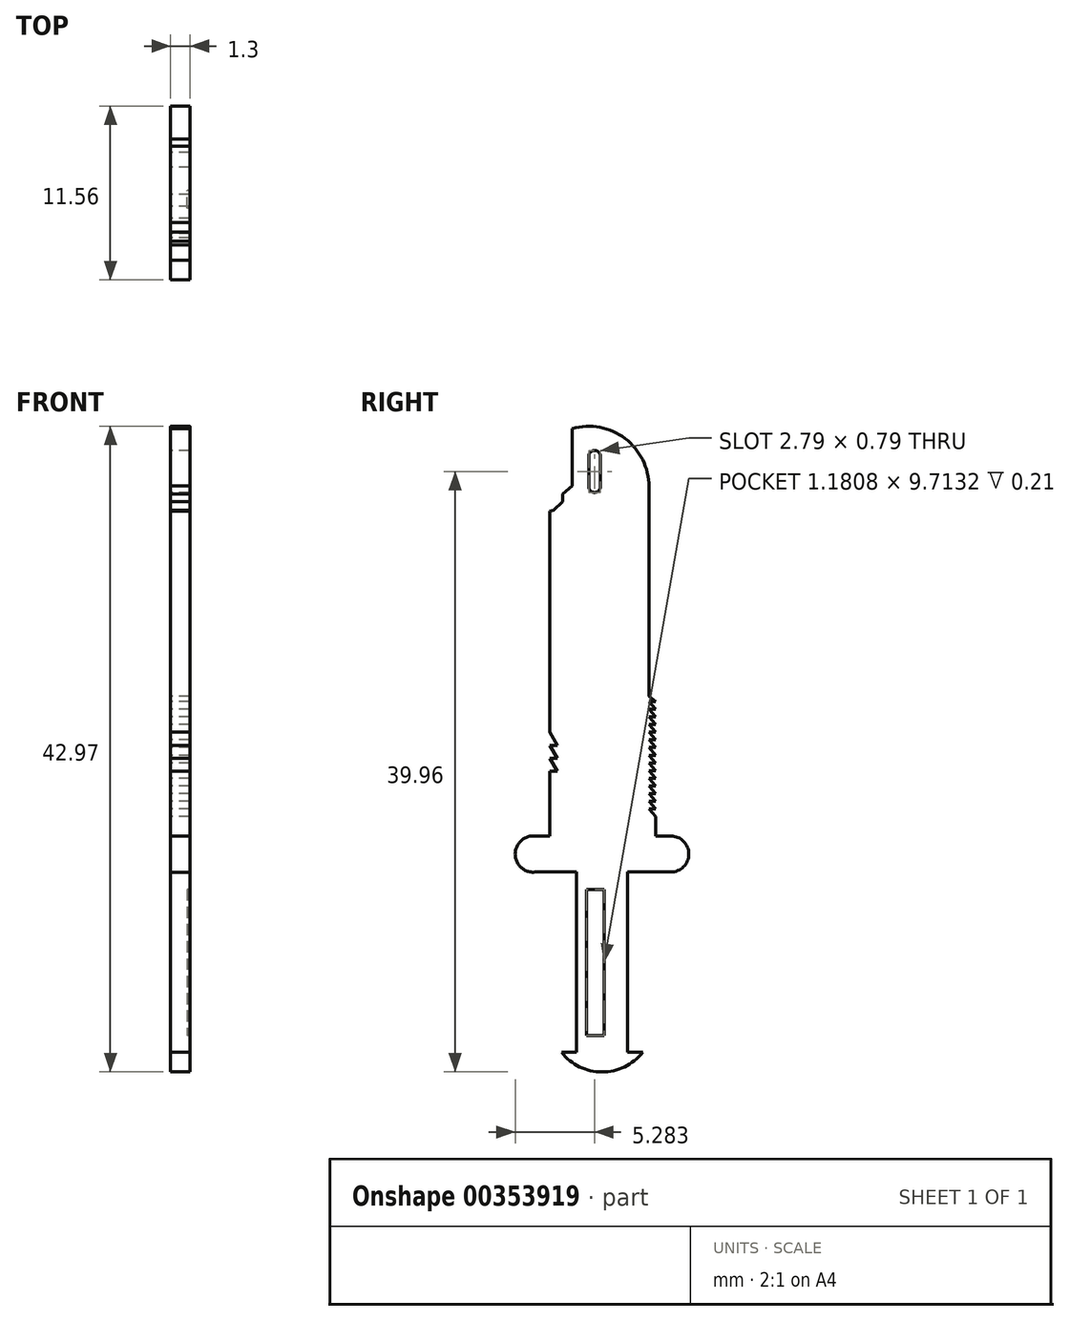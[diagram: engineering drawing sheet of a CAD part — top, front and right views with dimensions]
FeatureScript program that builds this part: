
annotation { "Feature Type Name" : "Feature", "Feature Type Description" : "" }
export const myFeature = defineFeature(function(context is Context, id is Id, definition is map)
    precondition{}
    {
        {
            var Q0;
            Q0=qCreatedBy(makeId("Right.planeOp"),FACE);
            var sketch = newSketch(context, id + "F0", { "sketchPlane" : qUnion([Q0])});
            skLineSegment(sketch, "E0", {"start": v(-45.92, 24.34) * mm, "end": v(-45.92, 12.34) * mm});
            skLineSegment(sketch, "E1", {"start": v(-45.92, 12.34) * mm, "end": v(-46.92, 12.34) * mm});
            skLineSegment(sketch, "E2", {"start": v(-41.52, 12.34) * mm, "end": v(-42.52, 12.34) * mm});
            skLineSegment(sketch, "E3", {"start": v(-42.52, 12.34) * mm, "end": v(-42.52, 24.34) * mm});
            skLineSegment(sketch, "E4", {"start": v(-47.7, 48.37) * mm, "end": v(-47.44, 48.43) * mm});
            skLineSegment(sketch, "E5", {"start": v(-47.44, 48.43) * mm, "end": v(-46.83, 49) * mm});
            skLineSegment(sketch, "E6", {"start": v(-46.83, 49) * mm, "end": v(-46.83, 49.5) * mm});
            skLineSegment(sketch, "E7", {"start": v(-46.83, 49.5) * mm, "end": v(-46.2, 50.05) * mm});
            skLineSegment(sketch, "E8", {"start": v(-46.2, 50.05) * mm, "end": v(-46.2, 50.86) * mm});
            skLineSegment(sketch, "E9", {"start": v(-46.2, 50.86) * mm, "end": v(-46.2, 53.86) * mm});
            skLineSegment(sketch, "E10", {"start": v(-46.2, 53.86) * mm, "end": v(-45.44, 53.86) * mm});
            skLineSegment(sketch, "E11", {"start": v(-45.44, 53.86) * mm, "end": v(-44.86, 53.5) * mm});
            skLineSegment(sketch, "E12", {"start": v(-44.86, 53.5) * mm, "end": v(-43.98, 52.87) * mm});
            skLineSegment(sketch, "E13", {"start": v(-43.98, 52.87) * mm, "end": v(-42.83, 51.88) * mm});
            skLineSegment(sketch, "E14", {"start": v(-42.83, 51.88) * mm, "end": v(-42.23, 50.74) * mm});
            skLineSegment(sketch, "E15", {"start": v(-42.23, 50.74) * mm, "end": v(-42.23, 49.66) * mm});
            skLineSegment(sketch, "E16", {"start": v(-42.23, 49.66) * mm, "end": v(-42.23, 48.37) * mm});
            skLineSegment(sketch, "E17", {"start": v(-42.23, 48.37) * mm, "end": v(-42.23, 47.61) * mm});
            skLineSegment(sketch, "E18", {"start": v(-42.23, 47.61) * mm, "end": v(-42.23, 36.92) * mm});
            skLineSegment(sketch, "E19", {"start": v(-42.23, 36.92) * mm, "end": v(-40.64, 35.69) * mm});
            skLineSegment(sketch, "E20", {"start": v(-40.64, 35.69) * mm, "end": v(-41.1, 35.7) * mm});
            skLineSegment(sketch, "E21", {"start": v(-41.1, 35.7) * mm, "end": v(-40.64, 35.17) * mm});
            skLineSegment(sketch, "E22", {"start": v(-40.64, 35.17) * mm, "end": v(-41.1, 35.17) * mm});
            skLineSegment(sketch, "E23", {"start": v(-41.1, 35.17) * mm, "end": v(-40.64, 34.66) * mm});
            skLineSegment(sketch, "E24", {"start": v(-40.64, 34.66) * mm, "end": v(-41.1, 34.66) * mm});
            skLineSegment(sketch, "E25", {"start": v(-41.1, 34.66) * mm, "end": v(-40.64, 34.15) * mm});
            skLineSegment(sketch, "E26", {"start": v(-40.64, 34.15) * mm, "end": v(-41.1, 34.15) * mm});
            skLineSegment(sketch, "E27", {"start": v(-41.1, 34.15) * mm, "end": v(-40.64, 33.64) * mm});
            skLineSegment(sketch, "E28", {"start": v(-40.64, 33.64) * mm, "end": v(-41.1, 33.64) * mm});
            skLineSegment(sketch, "E29", {"start": v(-41.1, 33.64) * mm, "end": v(-40.64, 33.14) * mm});
            skLineSegment(sketch, "E30", {"start": v(-40.64, 33.14) * mm, "end": v(-41.1, 33.14) * mm});
            skLineSegment(sketch, "E31", {"start": v(-41.1, 33.14) * mm, "end": v(-40.64, 32.63) * mm});
            skLineSegment(sketch, "E32", {"start": v(-40.64, 32.63) * mm, "end": v(-41.1, 32.63) * mm});
            skLineSegment(sketch, "E33", {"start": v(-41.1, 32.63) * mm, "end": v(-40.64, 32.12) * mm});
            skLineSegment(sketch, "E34", {"start": v(-40.64, 32.12) * mm, "end": v(-41.1, 32.12) * mm});
            skLineSegment(sketch, "E35", {"start": v(-41.1, 32.12) * mm, "end": v(-40.64, 31.6) * mm});
            skLineSegment(sketch, "E36", {"start": v(-40.64, 31.6) * mm, "end": v(-41.1, 31.6) * mm});
            skLineSegment(sketch, "E37", {"start": v(-41.1, 31.6) * mm, "end": v(-40.64, 31.1) * mm});
            skLineSegment(sketch, "E38", {"start": v(-40.64, 31.1) * mm, "end": v(-41.1, 31.1) * mm});
            skLineSegment(sketch, "E39", {"start": v(-41.1, 31.1) * mm, "end": v(-40.64, 30.6) * mm});
            skLineSegment(sketch, "E40", {"start": v(-40.64, 30.6) * mm, "end": v(-41.1, 30.6) * mm});
            skLineSegment(sketch, "E41", {"start": v(-41.1, 30.6) * mm, "end": v(-40.64, 30.08) * mm});
            skLineSegment(sketch, "E42", {"start": v(-40.64, 30.08) * mm, "end": v(-41.1, 30.08) * mm});
            skLineSegment(sketch, "E43", {"start": v(-41.1, 30.08) * mm, "end": v(-40.64, 29.58) * mm});
            skLineSegment(sketch, "E44", {"start": v(-40.64, 29.58) * mm, "end": v(-41.1, 29.58) * mm});
            skLineSegment(sketch, "E45", {"start": v(-41.1, 29.58) * mm, "end": v(-40.64, 29.07) * mm});
            skLineSegment(sketch, "E46", {"start": v(-40.64, 29.07) * mm, "end": v(-41.1, 29.07) * mm});
            skLineSegment(sketch, "E47", {"start": v(-41.1, 29.07) * mm, "end": v(-40.64, 28.56) * mm});
            skLineSegment(sketch, "E48", {"start": v(-40.64, 28.56) * mm, "end": v(-41.1, 28.56) * mm});
            skLineSegment(sketch, "E49", {"start": v(-41.1, 28.56) * mm, "end": v(-40.64, 28.05) * mm});
            skLineSegment(sketch, "E50", {"start": v(-40.64, 28.05) * mm, "end": v(-40.64, 26.74) * mm});
            skLineSegment(sketch, "E51", {"start": v(-47.7, 26.74) * mm, "end": v(-40.64, 26.74) * mm});
            skLineSegment(sketch, "E52", {"start": v(-45.92, 24.34) * mm, "end": v(-42.52, 24.34) * mm});
            skLineSegment(sketch, "E53", {"start": v(-45.92, 12.34) * mm, "end": v(-42.52, 12.34) * mm});
            skLineSegment(sketch, "E54", {"start": v(-41.1, 36.05) * mm, "end": v(-41.1, 50) * mm});
            skArc(sketch, "E55", {"start": v(-41.1, 50) * mm, "mid": v(-42.69, 53.2) * mm, "end": v(-46.2, 53.86) * mm});
            skLineSegment(sketch, "E56", {"start": v(-45.11, 50) * mm, "end": v(-45.11, 52) * mm});
            skArc(sketch, "E57", {"start": v(-45.11, 50) * mm, "mid": v(-44.72, 49.6) * mm, "end": v(-44.32, 50) * mm});
            skLineSegment(sketch, "E58", {"start": v(-44.32, 50) * mm, "end": v(-44.32, 52) * mm});
            skArc(sketch, "E59", {"start": v(-44.32, 52) * mm, "mid": v(-44.72, 52.4) * mm, "end": v(-45.11, 52) * mm});
            skLineSegment(sketch, "E60.bottom", {"start": v(-45.26, 23.19) * mm, "end": v(-44.07, 23.19) * mm});
            skLineSegment(sketch, "E60.top", {"start": v(-45.26, 13.47) * mm, "end": v(-44.07, 13.47) * mm});
            skLineSegment(sketch, "E60.left", {"start": v(-45.26, 23.19) * mm, "end": v(-45.26, 13.47) * mm});
            skLineSegment(sketch, "E60.right", {"start": v(-44.07, 23.19) * mm, "end": v(-44.07, 13.47) * mm});
            skLineSegment(sketch, "E61", {"start": v(-42.52, 23.19) * mm, "end": v(-42.92, 23.19) * mm});
            skLineSegment(sketch, "E62", {"start": v(-42.92, 23.19) * mm, "end": v(-42.52, 23.19) * mm});
            skLineSegment(sketch, "E63", {"start": v(-42.52, 23.19) * mm, "end": v(-42.52, 22.89) * mm});
            skLineSegment(sketch, "E64", {"start": v(-42.52, 22.89) * mm, "end": v(-42.92, 22.89) * mm});
            skLineSegment(sketch, "E65", {"start": v(-42.92, 22.89) * mm, "end": v(-42.52, 22.89) * mm});
            skLineSegment(sketch, "E66", {"start": v(-42.52, 22.89) * mm, "end": v(-42.52, 22.59) * mm});
            skLineSegment(sketch, "E67", {"start": v(-42.52, 22.59) * mm, "end": v(-42.92, 22.59) * mm});
            skLineSegment(sketch, "E68", {"start": v(-42.92, 22.59) * mm, "end": v(-42.52, 22.59) * mm});
            skLineSegment(sketch, "E69", {"start": v(-42.52, 22.59) * mm, "end": v(-42.52, 22.29) * mm});
            skLineSegment(sketch, "E70", {"start": v(-42.52, 22.29) * mm, "end": v(-42.92, 22.29) * mm});
            skLineSegment(sketch, "E71", {"start": v(-42.92, 22.29) * mm, "end": v(-42.52, 22.29) * mm});
            skLineSegment(sketch, "E72", {"start": v(-42.52, 22.29) * mm, "end": v(-42.52, 21.99) * mm});
            skLineSegment(sketch, "E73", {"start": v(-42.52, 21.99) * mm, "end": v(-42.92, 21.99) * mm});
            skLineSegment(sketch, "E74", {"start": v(-42.92, 21.99) * mm, "end": v(-42.52, 21.99) * mm});
            skLineSegment(sketch, "E75", {"start": v(-42.52, 21.99) * mm, "end": v(-42.52, 21.69) * mm});
            skLineSegment(sketch, "E76", {"start": v(-42.52, 21.69) * mm, "end": v(-42.92, 21.69) * mm});
            skLineSegment(sketch, "E77", {"start": v(-42.92, 21.69) * mm, "end": v(-42.52, 21.69) * mm});
            skLineSegment(sketch, "E78", {"start": v(-42.52, 21.69) * mm, "end": v(-42.52, 21.39) * mm});
            skLineSegment(sketch, "E79", {"start": v(-42.52, 21.39) * mm, "end": v(-42.92, 21.39) * mm});
            skLineSegment(sketch, "E80", {"start": v(-42.92, 21.39) * mm, "end": v(-42.52, 21.39) * mm});
            skLineSegment(sketch, "E81", {"start": v(-42.52, 21.39) * mm, "end": v(-42.52, 21.09) * mm});
            skLineSegment(sketch, "E82", {"start": v(-42.52, 21.09) * mm, "end": v(-42.92, 21.09) * mm});
            skLineSegment(sketch, "E83", {"start": v(-42.92, 21.09) * mm, "end": v(-42.52, 21.09) * mm});
            skLineSegment(sketch, "E84", {"start": v(-42.52, 21.09) * mm, "end": v(-42.52, 20.79) * mm});
            skLineSegment(sketch, "E85", {"start": v(-42.52, 20.79) * mm, "end": v(-42.92, 20.79) * mm});
            skLineSegment(sketch, "E86", {"start": v(-42.92, 20.79) * mm, "end": v(-42.52, 20.79) * mm});
            skLineSegment(sketch, "E87", {"start": v(-42.52, 20.79) * mm, "end": v(-42.52, 20.49) * mm});
            skLineSegment(sketch, "E88", {"start": v(-42.52, 20.49) * mm, "end": v(-42.92, 20.49) * mm});
            skLineSegment(sketch, "E89", {"start": v(-42.92, 20.49) * mm, "end": v(-42.52, 20.49) * mm});
            skLineSegment(sketch, "E90", {"start": v(-42.52, 20.49) * mm, "end": v(-42.52, 20.19) * mm});
            skLineSegment(sketch, "E91", {"start": v(-42.52, 20.19) * mm, "end": v(-42.92, 20.19) * mm});
            skLineSegment(sketch, "E92", {"start": v(-42.92, 20.19) * mm, "end": v(-42.52, 20.19) * mm});
            skLineSegment(sketch, "E93", {"start": v(-42.52, 20.19) * mm, "end": v(-42.52, 19.89) * mm});
            skLineSegment(sketch, "E94", {"start": v(-42.52, 19.89) * mm, "end": v(-42.92, 19.89) * mm});
            skLineSegment(sketch, "E95", {"start": v(-42.92, 19.89) * mm, "end": v(-42.52, 19.89) * mm});
            skLineSegment(sketch, "E96", {"start": v(-42.52, 19.89) * mm, "end": v(-42.52, 19.59) * mm});
            skLineSegment(sketch, "E97", {"start": v(-42.52, 19.59) * mm, "end": v(-42.92, 19.59) * mm});
            skLineSegment(sketch, "E98", {"start": v(-42.92, 19.59) * mm, "end": v(-42.52, 19.59) * mm});
            skLineSegment(sketch, "E99", {"start": v(-42.52, 19.59) * mm, "end": v(-42.52, 19.28) * mm});
            skLineSegment(sketch, "E100", {"start": v(-42.52, 19.28) * mm, "end": v(-42.92, 19.28) * mm});
            skLineSegment(sketch, "E101", {"start": v(-42.92, 19.28) * mm, "end": v(-42.52, 19.28) * mm});
            skLineSegment(sketch, "E102", {"start": v(-42.52, 19.28) * mm, "end": v(-42.52, 18.98) * mm});
            skLineSegment(sketch, "E103", {"start": v(-42.52, 18.98) * mm, "end": v(-42.92, 18.98) * mm});
            skLineSegment(sketch, "E104", {"start": v(-42.92, 18.98) * mm, "end": v(-42.52, 18.98) * mm});
            skLineSegment(sketch, "E105", {"start": v(-42.52, 18.98) * mm, "end": v(-42.52, 18.68) * mm});
            skLineSegment(sketch, "E106", {"start": v(-42.52, 18.68) * mm, "end": v(-42.92, 18.68) * mm});
            skLineSegment(sketch, "E107", {"start": v(-42.92, 18.68) * mm, "end": v(-42.52, 18.68) * mm});
            skLineSegment(sketch, "E108", {"start": v(-42.52, 18.68) * mm, "end": v(-42.52, 18.38) * mm});
            skLineSegment(sketch, "E109", {"start": v(-42.52, 18.38) * mm, "end": v(-42.92, 18.38) * mm});
            skLineSegment(sketch, "E110", {"start": v(-42.92, 18.38) * mm, "end": v(-42.52, 18.38) * mm});
            skLineSegment(sketch, "E111", {"start": v(-42.52, 18.38) * mm, "end": v(-42.52, 18.08) * mm});
            skLineSegment(sketch, "E112", {"start": v(-42.52, 18.08) * mm, "end": v(-42.92, 18.08) * mm});
            skLineSegment(sketch, "E113", {"start": v(-42.92, 18.08) * mm, "end": v(-42.52, 18.08) * mm});
            skLineSegment(sketch, "E114", {"start": v(-42.52, 18.08) * mm, "end": v(-42.52, 17.78) * mm});
            skLineSegment(sketch, "E115", {"start": v(-42.52, 17.78) * mm, "end": v(-42.92, 17.78) * mm});
            skLineSegment(sketch, "E116", {"start": v(-42.92, 17.78) * mm, "end": v(-42.52, 17.78) * mm});
            skLineSegment(sketch, "E117", {"start": v(-42.52, 17.78) * mm, "end": v(-42.52, 17.48) * mm});
            skLineSegment(sketch, "E118", {"start": v(-42.52, 17.48) * mm, "end": v(-42.92, 17.48) * mm});
            skLineSegment(sketch, "E119", {"start": v(-42.92, 17.48) * mm, "end": v(-42.52, 17.48) * mm});
            skLineSegment(sketch, "E120", {"start": v(-42.52, 17.48) * mm, "end": v(-42.52, 17.18) * mm});
            skLineSegment(sketch, "E121", {"start": v(-42.52, 17.18) * mm, "end": v(-42.92, 17.18) * mm});
            skLineSegment(sketch, "E122", {"start": v(-42.92, 17.18) * mm, "end": v(-42.52, 17.18) * mm});
            skLineSegment(sketch, "E123", {"start": v(-42.52, 17.18) * mm, "end": v(-42.52, 16.89) * mm});
            skLineSegment(sketch, "E124", {"start": v(-42.52, 16.89) * mm, "end": v(-42.92, 16.89) * mm});
            skLineSegment(sketch, "E125", {"start": v(-42.92, 16.89) * mm, "end": v(-42.52, 16.89) * mm});
            skLineSegment(sketch, "E126", {"start": v(-42.52, 16.89) * mm, "end": v(-42.52, 16.59) * mm});
            skLineSegment(sketch, "E127", {"start": v(-42.52, 16.59) * mm, "end": v(-42.92, 16.59) * mm});
            skLineSegment(sketch, "E128", {"start": v(-42.92, 16.59) * mm, "end": v(-42.52, 16.59) * mm});
            skLineSegment(sketch, "E129", {"start": v(-42.52, 16.59) * mm, "end": v(-42.52, 16.29) * mm});
            skLineSegment(sketch, "E130", {"start": v(-42.52, 16.29) * mm, "end": v(-42.92, 16.29) * mm});
            skLineSegment(sketch, "E131", {"start": v(-42.92, 16.29) * mm, "end": v(-42.52, 16.29) * mm});
            skLineSegment(sketch, "E132", {"start": v(-42.52, 16.29) * mm, "end": v(-42.52, 15.99) * mm});
            skLineSegment(sketch, "E133", {"start": v(-42.52, 15.99) * mm, "end": v(-42.92, 15.99) * mm});
            skLineSegment(sketch, "E134", {"start": v(-42.92, 15.99) * mm, "end": v(-42.52, 15.99) * mm});
            skLineSegment(sketch, "E135", {"start": v(-42.52, 15.99) * mm, "end": v(-42.52, 15.69) * mm});
            skLineSegment(sketch, "E136", {"start": v(-42.52, 15.69) * mm, "end": v(-42.92, 15.69) * mm});
            skLineSegment(sketch, "E137", {"start": v(-42.92, 15.69) * mm, "end": v(-42.52, 15.69) * mm});
            skLineSegment(sketch, "E138", {"start": v(-42.52, 15.69) * mm, "end": v(-42.52, 15.39) * mm});
            skLineSegment(sketch, "E139", {"start": v(-42.52, 15.39) * mm, "end": v(-42.92, 15.39) * mm});
            skLineSegment(sketch, "E140", {"start": v(-42.92, 15.39) * mm, "end": v(-42.52, 15.39) * mm});
            skLineSegment(sketch, "E141", {"start": v(-42.52, 15.39) * mm, "end": v(-42.52, 15.09) * mm});
            skLineSegment(sketch, "E142", {"start": v(-42.52, 15.09) * mm, "end": v(-42.92, 15.09) * mm});
            skLineSegment(sketch, "E143", {"start": v(-42.92, 15.09) * mm, "end": v(-42.52, 15.09) * mm});
            skLineSegment(sketch, "E144", {"start": v(-42.52, 15.09) * mm, "end": v(-42.52, 14.79) * mm});
            skLineSegment(sketch, "E145", {"start": v(-42.52, 14.79) * mm, "end": v(-42.92, 14.79) * mm});
            skLineSegment(sketch, "E146", {"start": v(-42.92, 14.79) * mm, "end": v(-42.52, 14.79) * mm});
            skLineSegment(sketch, "E147", {"start": v(-42.52, 14.79) * mm, "end": v(-42.52, 14.49) * mm});
            skLineSegment(sketch, "E148", {"start": v(-42.52, 14.49) * mm, "end": v(-42.92, 14.49) * mm});
            skArc(sketch, "E149", {"start": v(-42.92, 23.19) * mm, "mid": v(-43.07, 23.04) * mm, "end": v(-42.92, 22.89) * mm});
            skArc(sketch, "E150", {"start": v(-42.92, 22.89) * mm, "mid": v(-43.07, 22.74) * mm, "end": v(-42.92, 22.59) * mm});
            skArc(sketch, "E151", {"start": v(-42.92, 22.59) * mm, "mid": v(-43.07, 22.44) * mm, "end": v(-42.92, 22.29) * mm});
            skArc(sketch, "E152", {"start": v(-42.92, 22.29) * mm, "mid": v(-43.07, 22.14) * mm, "end": v(-42.92, 21.99) * mm});
            skArc(sketch, "E153", {"start": v(-42.92, 21.99) * mm, "mid": v(-43.07, 21.84) * mm, "end": v(-42.92, 21.69) * mm});
            skArc(sketch, "E154", {"start": v(-42.92, 21.69) * mm, "mid": v(-43.07, 21.54) * mm, "end": v(-42.92, 21.39) * mm});
            skArc(sketch, "E155", {"start": v(-42.92, 21.39) * mm, "mid": v(-43.07, 21.24) * mm, "end": v(-42.92, 21.09) * mm});
            skArc(sketch, "E156", {"start": v(-42.92, 21.09) * mm, "mid": v(-43.07, 20.94) * mm, "end": v(-42.92, 20.79) * mm});
            skArc(sketch, "E157", {"start": v(-42.92, 20.79) * mm, "mid": v(-43.07, 20.64) * mm, "end": v(-42.92, 20.49) * mm});
            skArc(sketch, "E158", {"start": v(-42.92, 20.49) * mm, "mid": v(-43.07, 20.34) * mm, "end": v(-42.92, 20.19) * mm});
            skArc(sketch, "E159", {"start": v(-42.92, 20.19) * mm, "mid": v(-43.07, 20.04) * mm, "end": v(-42.92, 19.89) * mm});
            skArc(sketch, "E160", {"start": v(-42.92, 19.89) * mm, "mid": v(-43.07, 19.74) * mm, "end": v(-42.92, 19.59) * mm});
            skArc(sketch, "E161", {"start": v(-42.92, 19.59) * mm, "mid": v(-43.07, 19.43) * mm, "end": v(-42.92, 19.28) * mm});
            skArc(sketch, "E162", {"start": v(-42.92, 19.28) * mm, "mid": v(-43.07, 19.13) * mm, "end": v(-42.92, 18.98) * mm});
            skArc(sketch, "E163", {"start": v(-42.92, 18.98) * mm, "mid": v(-43.07, 18.83) * mm, "end": v(-42.92, 18.68) * mm});
            skArc(sketch, "E164", {"start": v(-42.92, 18.68) * mm, "mid": v(-43.07, 18.53) * mm, "end": v(-42.92, 18.38) * mm});
            skArc(sketch, "E165", {"start": v(-42.92, 18.38) * mm, "mid": v(-43.07, 18.23) * mm, "end": v(-42.92, 18.08) * mm});
            skArc(sketch, "E166", {"start": v(-42.92, 18.08) * mm, "mid": v(-43.07, 17.93) * mm, "end": v(-42.92, 17.78) * mm});
            skArc(sketch, "E167", {"start": v(-42.92, 17.78) * mm, "mid": v(-43.07, 17.63) * mm, "end": v(-42.92, 17.48) * mm});
            skArc(sketch, "E168", {"start": v(-42.92, 17.48) * mm, "mid": v(-43.07, 17.33) * mm, "end": v(-42.92, 17.18) * mm});
            skArc(sketch, "E169", {"start": v(-42.92, 17.18) * mm, "mid": v(-43.07, 17.03) * mm, "end": v(-42.92, 16.89) * mm});
            skArc(sketch, "E170", {"start": v(-42.92, 16.89) * mm, "mid": v(-43.07, 16.74) * mm, "end": v(-42.92, 16.59) * mm});
            skArc(sketch, "E171", {"start": v(-42.92, 16.59) * mm, "mid": v(-43.07, 16.44) * mm, "end": v(-42.92, 16.29) * mm});
            skArc(sketch, "E172", {"start": v(-42.92, 16.29) * mm, "mid": v(-43.07, 16.14) * mm, "end": v(-42.92, 15.99) * mm});
            skArc(sketch, "E173", {"start": v(-42.91, 15.98) * mm, "mid": v(-43.07, 15.84) * mm, "end": v(-42.92, 15.69) * mm});
            skArc(sketch, "E174", {"start": v(-42.92, 15.69) * mm, "mid": v(-43.07, 15.54) * mm, "end": v(-42.92, 15.39) * mm});
            skArc(sketch, "E175", {"start": v(-42.92, 15.39) * mm, "mid": v(-43.07, 15.24) * mm, "end": v(-42.92, 15.09) * mm});
            skArc(sketch, "E176", {"start": v(-42.92, 15.09) * mm, "mid": v(-43.07, 14.94) * mm, "end": v(-42.92, 14.79) * mm});
            skArc(sketch, "E177", {"start": v(-42.92, 14.79) * mm, "mid": v(-43.07, 14.64) * mm, "end": v(-42.92, 14.49) * mm});
            skLineSegment(sketch, "E178", {"start": v(-47.7, 31.05) * mm, "end": v(-47.2, 31.05) * mm});
            skLineSegment(sketch, "E179", {"start": v(-47.2, 31.05) * mm, "end": v(-47.7, 31.92) * mm});
            skLineSegment(sketch, "E180", {"start": v(-47.7, 31.92) * mm, "end": v(-47.2, 31.92) * mm});
            skLineSegment(sketch, "E181", {"start": v(-47.2, 31.92) * mm, "end": v(-47.7, 32.78) * mm});
            skLineSegment(sketch, "E182", {"start": v(-47.7, 32.78) * mm, "end": v(-47.2, 32.78) * mm});
            skLineSegment(sketch, "E183", {"start": v(-47.2, 32.78) * mm, "end": v(-47.7, 33.65) * mm});
            skLineSegment(sketch, "E184", {"start": v(-47.7, 31.05) * mm, "end": v(-47.7, 26.74) * mm});
            skLineSegment(sketch, "E185", {"start": v(-47.7, 33.65) * mm, "end": v(-47.7, 48.37) * mm});
            skLineSegment(sketch, "E186", {"start": v(-40.64, 26.74) * mm, "end": v(-39.64, 26.74) * mm});
            skLineSegment(sketch, "E187", {"start": v(-39.64, 26.74) * mm, "end": v(-39.64, 24.34) * mm});
            skLineSegment(sketch, "E188", {"start": v(-47.7, 26.74) * mm, "end": v(-48.7, 26.74) * mm});
            skLineSegment(sketch, "E189", {"start": v(-48.7, 26.74) * mm, "end": v(-48.7, 24.34) * mm});
            skArc(sketch, "E190", {"start": v(-48.7, 26.74) * mm, "mid": v(-50, 25.54) * mm, "end": v(-48.7, 24.34) * mm});
            skArc(sketch, "E191", {"start": v(-39.64, 24.34) * mm, "mid": v(-38.44, 25.54) * mm, "end": v(-39.64, 26.74) * mm});
            skLineSegment(sketch, "E192", {"start": v(-48.7, 24.34) * mm, "end": v(-45.92, 24.34) * mm});
            skLineSegment(sketch, "E193", {"start": v(-42.52, 24.34) * mm, "end": v(-39.64, 24.34) * mm});
            skArc(sketch, "E194", {"start": v(-46.92, 12.34) * mm, "mid": v(-44.22, 11.04) * mm, "end": v(-41.52, 12.34) * mm});
            skSolve(sketch);
        }
        {
            var Q0;
            Q0 = qSketchRegion(id + "F0", true);
            extrude(context, id + "F1", {"entities" : qUnion([Q0]), "depth" : 1.3 * mm});
        }
        {
            var Q0;
            Q0=qCreatedBy(makeId("Right.planeOp"),FACE);
            var sketch = newSketch(context, id + "F2", { "sketchPlane" : qUnion([Q0])});
            skLineSegment(sketch, "E195.bottom", {"start": v(-45.32, 23.35) * mm, "end": v(-43.98, 23.35) * mm});
            skLineSegment(sketch, "E195.top", {"start": v(-45.32, 13.29) * mm, "end": v(-43.98, 13.29) * mm});
            skLineSegment(sketch, "E195.left", {"start": v(-45.32, 23.35) * mm, "end": v(-45.32, 13.29) * mm});
            skLineSegment(sketch, "E195.right", {"start": v(-43.98, 23.35) * mm, "end": v(-43.98, 13.29) * mm});
            skSolve(sketch);
        }
        {
            var Q0;
            Q0 = qSketchRegion(id + "F2", true);
            extrude(context, id + "F3", {"entities" : qUnion([Q0]), "operationType" : NewBodyOperationType.ADD, "depth" : 1.09 * mm});
        }
    });
